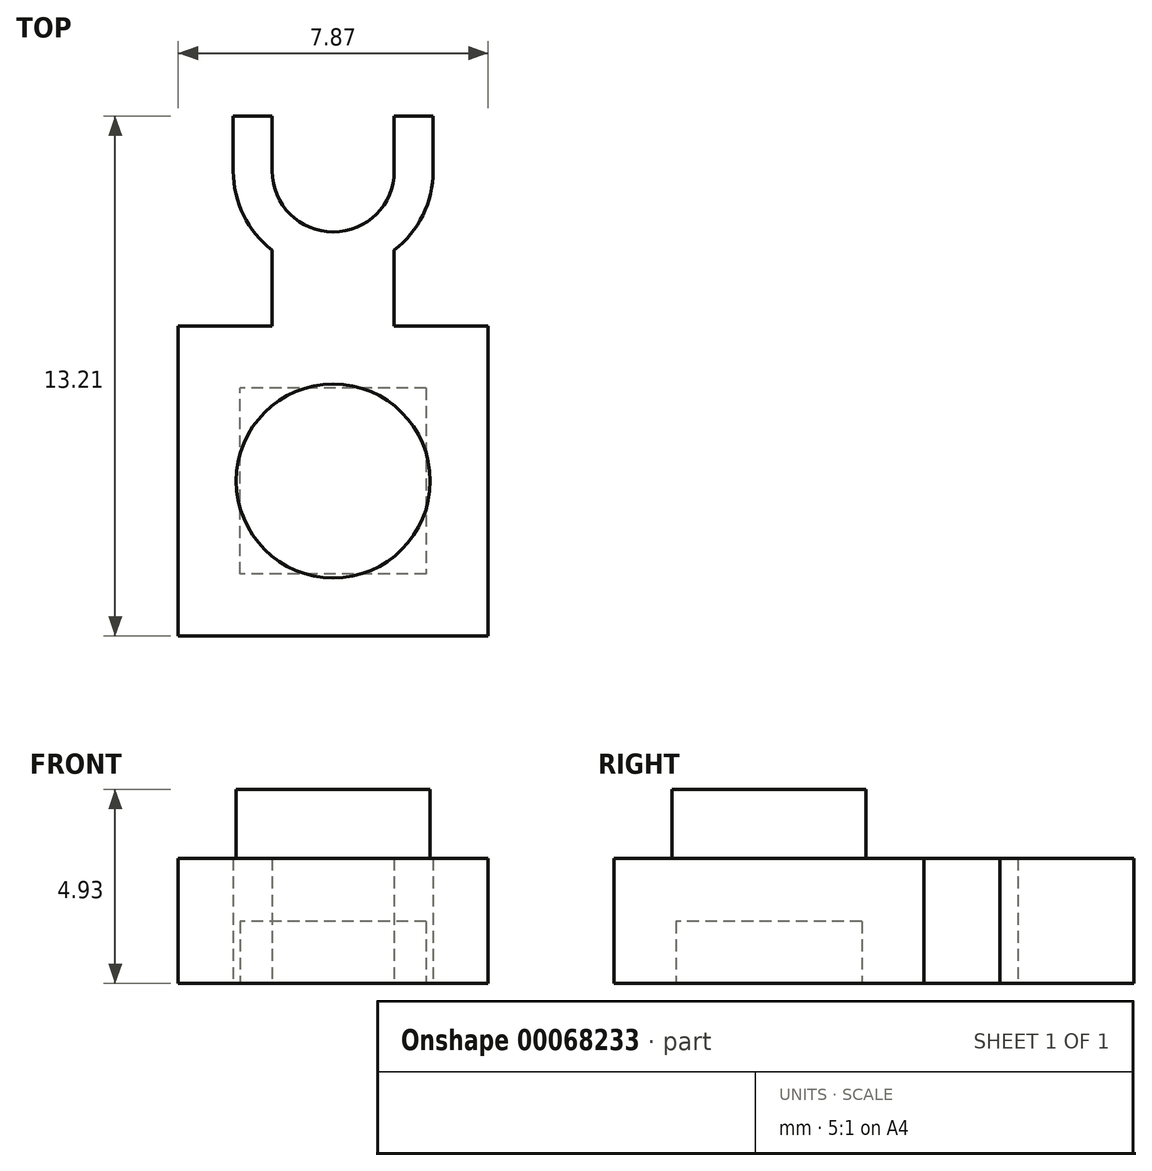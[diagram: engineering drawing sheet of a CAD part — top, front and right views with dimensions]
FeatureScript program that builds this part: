
annotation { "Feature Type Name" : "Feature", "Feature Type Description" : "" }
export const myFeature = defineFeature(function(context is Context, id is Id, definition is map)
    precondition{}
    {
        {
            var Q0;
            Q0=qCreatedBy(makeId("Top.planeOp"),FACE);
            var sketch = newSketch(context, id + "F0", { "sketchPlane" : qUnion([Q0])});
            skLineSegment(sketch, "E0.bottom", {"start": v(0, 0) * mm, "end": v(7.87, 0) * mm});
            skLineSegment(sketch, "E0.left", {"start": v(0, 0) * mm, "end": v(0, 7.87) * mm});
            skLineSegment(sketch, "E0.right", {"start": v(7.87, 0) * mm, "end": v(7.87, 7.87) * mm});
            skPoint(sketch, "E1.endSnap0", {"position": v(-28.75, 21.53) * mm});
            skArc(sketch, "E2.0", {"start": v(2.39, 11.81) * mm, "mid": v(3.94, 10.26) * mm, "end": v(5.49, 11.81) * mm});
            skLineSegment(sketch, "E3", {"start": v(1.4, 11.81) * mm, "end": v(1.4, 13.2) * mm});
            skLineSegment(sketch, "E4", {"start": v(1.4, 13.2) * mm, "end": v(2.39, 13.2) * mm});
            skLineSegment(sketch, "E5", {"start": v(2.39, 13.2) * mm, "end": v(2.39, 11.81) * mm});
            skLineSegment(sketch, "E6", {"start": v(5.49, 11.81) * mm, "end": v(5.49, 13.2) * mm});
            skLineSegment(sketch, "E7", {"start": v(5.49, 13.2) * mm, "end": v(6.48, 13.2) * mm});
            skLineSegment(sketch, "E8", {"start": v(6.48, 13.2) * mm, "end": v(6.48, 11.81) * mm});
            skLineSegment(sketch, "E9", {"start": v(2.39, 7.87) * mm, "end": v(2.39, 9.8) * mm});
            skLineSegment(sketch, "E10", {"start": v(5.49, 9.8) * mm, "end": v(5.49, 7.87) * mm});
            skLineSegment(sketch, "E11", {"start": v(0, 7.87) * mm, "end": v(2.39, 7.87) * mm});
            skLineSegment(sketch, "E12", {"start": v(5.49, 7.87) * mm, "end": v(7.87, 7.87) * mm});
            skArc(sketch, "E13", {"start": v(1.4, 11.81) * mm, "mid": v(1.66, 10.69) * mm, "end": v(2.39, 9.8) * mm});
            skArc(sketch, "E14", {"start": v(5.49, 9.8) * mm, "mid": v(6.22, 10.69) * mm, "end": v(6.48, 11.81) * mm});
            skSolve(sketch);
        }
        {
            var Q0;
            Q0 = qSketchRegion(id + "F0", true);
            extrude(context, id + "F1", {"entities" : qUnion([Q0]), "depth" : 3.17 * mm});
        }
        {
            var Q0;
            Q0=makeQuery(id+"F1.opExtrude","CAP_FACE",FACE,{"disambiguationData":[OSD([sQuery(id+"F0.wireOp",EDGE,"E0.bottom"),sQuery(id+"F0.wireOp",EDGE,"E0.left"),sQuery(id+"F0.wireOp",EDGE,"E0.right"),sQuery(id+"F0.wireOp",EDGE,"E2.0"),sQuery(id+"F0.wireOp",EDGE,"E3"),sQuery(id+"F0.wireOp",EDGE,"E4"),sQuery(id+"F0.wireOp",EDGE,"E5"),sQuery(id+"F0.wireOp",EDGE,"E6"),sQuery(id+"F0.wireOp",EDGE,"E7"),sQuery(id+"F0.wireOp",EDGE,"E8"),sQuery(id+"F0.wireOp",EDGE,"E9"),sQuery(id+"F0.wireOp",EDGE,"E10"),sQuery(id+"F0.wireOp",EDGE,"E11"),sQuery(id+"F0.wireOp",EDGE,"E12"),sQuery(id+"F0.wireOp",EDGE,"E13"),sQuery(id+"F0.wireOp",EDGE,"E14")])],"isStart":false});
            var sketch = newSketch(context, id + "F2", { "sketchPlane" : qUnion([Q0])});
            skLineSegment(sketch, "E15", {"start": v(0, 3.94) * mm, "end": v(7.87, 3.94) * mm});
            skCircle(sketch, "E16", {"center": v(3.94, 3.94) * mm, "radius": 2.46 * mm});
            skSolve(sketch);
        }
        {
            var Q0;
            Q0 = qSketchRegion(id + "F2", true);
            extrude(context, id + "F3", {"entities" : qUnion([Q0]), "operationType" : NewBodyOperationType.ADD, "depth" : 1.75 * mm});
        }
        {
            var Q0;
            Q0=makeQuery(id+"F1.opExtrude","CAP_FACE",FACE,{"disambiguationData":[OSD([sQuery(id+"F0.wireOp",EDGE,"E0.bottom"),sQuery(id+"F0.wireOp",EDGE,"E0.left"),sQuery(id+"F0.wireOp",EDGE,"E0.right"),sQuery(id+"F0.wireOp",EDGE,"E2.0"),sQuery(id+"F0.wireOp",EDGE,"E3"),sQuery(id+"F0.wireOp",EDGE,"E4"),sQuery(id+"F0.wireOp",EDGE,"E5"),sQuery(id+"F0.wireOp",EDGE,"E6"),sQuery(id+"F0.wireOp",EDGE,"E7"),sQuery(id+"F0.wireOp",EDGE,"E8"),sQuery(id+"F0.wireOp",EDGE,"E9"),sQuery(id+"F0.wireOp",EDGE,"E10"),sQuery(id+"F0.wireOp",EDGE,"E11"),sQuery(id+"F0.wireOp",EDGE,"E12"),sQuery(id+"F0.wireOp",EDGE,"E13"),sQuery(id+"F0.wireOp",EDGE,"E14")])],"isStart":true});
            var sketch = newSketch(context, id + "F4", { "sketchPlane" : qUnion([Q0])});
            skLineSegment(sketch, "E17.0", {"start": v(6.3, -1.57) * mm, "end": v(1.57, -1.57) * mm});
            skLineSegment(sketch, "E17.1", {"start": v(6.3, -6.3) * mm, "end": v(6.3, -1.57) * mm});
            skLineSegment(sketch, "E17.2", {"start": v(1.57, -1.57) * mm, "end": v(1.57, -6.3) * mm});
            skLineSegment(sketch, "E18", {"start": v(6.3, -6.3) * mm, "end": v(1.57, -6.3) * mm});
            skSolve(sketch);
        }
        {
            var Q0;
            Q0 = qSketchRegion(id + "F4", true);
            extrude(context, id + "F5", {"entities" : qUnion([Q0]), "operationType" : NewBodyOperationType.REMOVE, "oppositeDirection" : true, "depth" : 1.57 * mm});
        }
    });
